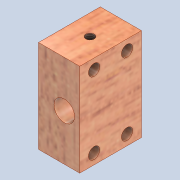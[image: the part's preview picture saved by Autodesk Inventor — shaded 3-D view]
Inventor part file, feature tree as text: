
AUTODESK INVENTOR PART (.ipt)
format: ipt  version: 2020 (Build 240168000, 168)  size: 165,888 bytes
history: native  units: mm
features: sketch x4, extrude x3, pattern_linear x1, hole x1
ambient origin geometry x8: Origin, YZ Plane, XZ Plane, XY Plane, X Axis, Y Axis, Z Axis, Center Point
bodies: Solid1 (feature_tree)
feature tree (9):
  extrude  "Extrusion1"  Depth=45.0mm
  extrude  "Extrusion2"  Depth=10.0mm
  extrude  "Extrusion3"  TaperAngle=0.0deg  [1 undecoded]
  pattern_linear  "Rectangular Pattern1"  Spacing1=5.5mm  [1 undecoded]
  hole  "Hole1"  [1 undecoded]
  sketch  "Sketch1"  dims[d0=20.0mm d1=45.0mm]
  sketch  "Sketch3"  dims[d2=30.0mm d3=0.0mm d4=10.0mm]
  sketch  "Sketch4"  dims[d5=7.5mm d6=0.0mm d7=0.0mm]
  sketch  "Sketch5"  dims[d8=5.5mm d9=5.5mm d10=7.0mm d11=5.0mm d12=5.0mm d13=7.0mm d14=0.0mm d15=0.0mm d16=35.0mm d17=16.0mm d18=20.0mm d20=16.0mm d21=20.0mm d23=35.0mm d24=4.134mm d25=45.0mm d26=4.0mm d27=2.0mm d28=90.0deg d29=8.0mm d30=20.594885mm]
note: 3 required parameter values undecoded (feature->parameter linkage not recoverable at this tier; creation-order binding heuristic only, values carry confidence <= 0.55)
